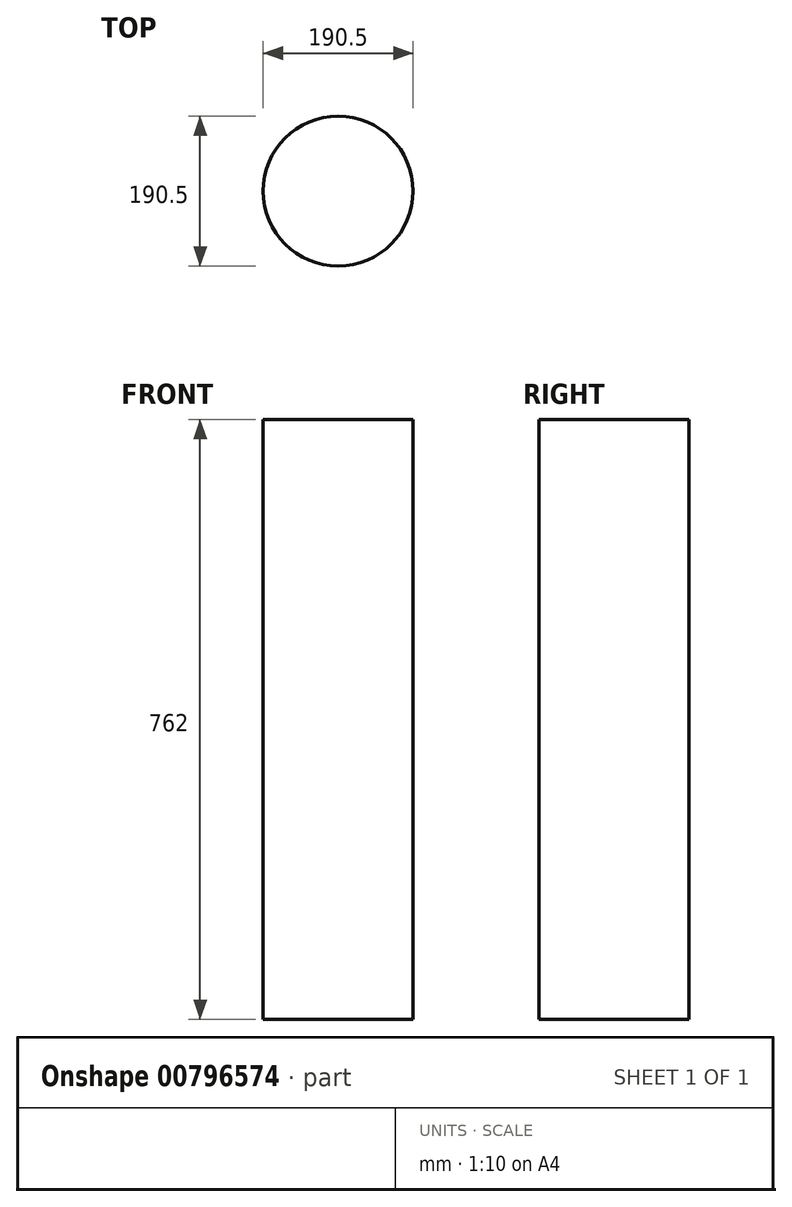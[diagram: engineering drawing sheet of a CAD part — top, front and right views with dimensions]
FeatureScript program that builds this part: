
annotation { "Feature Type Name" : "Feature", "Feature Type Description" : "" }
export const myFeature = defineFeature(function(context is Context, id is Id, definition is map)
    precondition{}
    {
        {
            var Q0;
            Q0=qCreatedBy(makeId("Top.planeOp"),FACE);
            var sketch = newSketch(context, id + "F0", { "sketchPlane" : qUnion([Q0])});
            skCircle(sketch, "E0", {"center": v(1.3, 26.07) * mm, "radius": 95.25 * mm});
            skPoint(sketch, "E0.first.point", {"position": v(-80.56, 74.75) * mm});
            skPoint(sketch, "E0.second.point", {"position": v(-93.07, 13.23) * mm});
            skPoint(sketch, "E0.third.point", {"position": v(63.35, -46.2) * mm});
            skSolve(sketch);
        }
        {
            var Q0;
            Q0 = qSketchRegion(id + "F0", true);
            extrude(context, id + "F1", {"entities" : qUnion([Q0]), "endBound" : BoundingType.SYMMETRIC, "depth" : 762 * mm, "offsetDistance" : 25.4 * mm});
        }
    });
